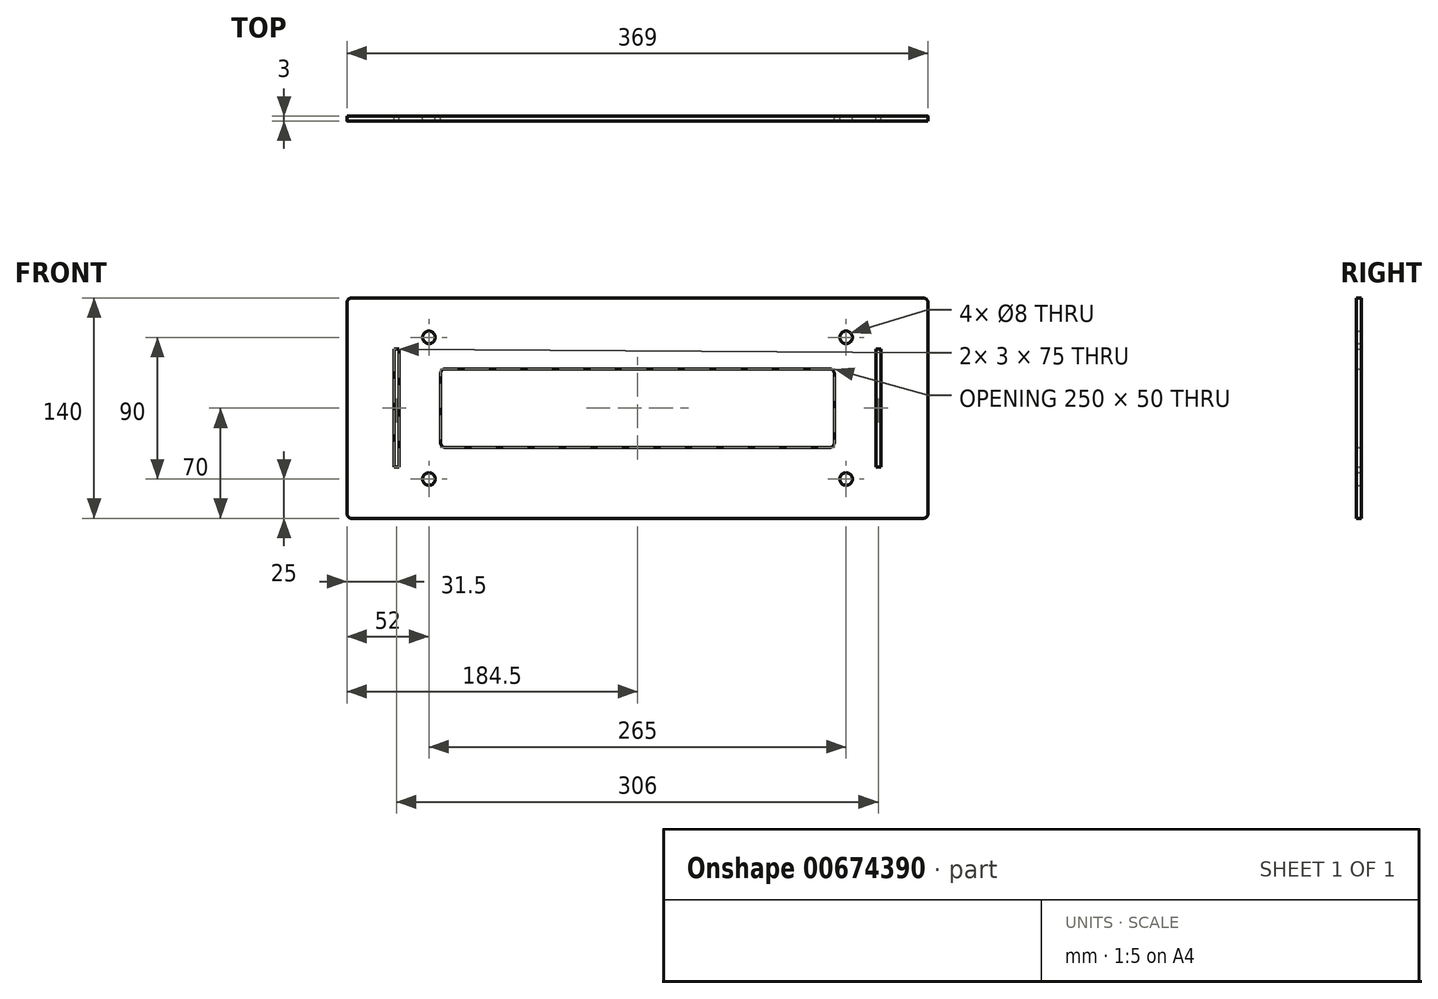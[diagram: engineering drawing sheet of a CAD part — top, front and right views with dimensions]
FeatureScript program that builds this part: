
annotation { "Feature Type Name" : "Feature", "Feature Type Description" : "" }
export const myFeature = defineFeature(function(context is Context, id is Id, definition is map)
    precondition{}
    {
        {
            var Q0;
            Q0=qCreatedBy(makeId("Front.planeOp"),FACE);
            var sketch = newSketch(context, id + "F0", { "sketchPlane" : qUnion([Q0])});
            skLineSegment(sketch, "E0.bottom", {"start": v(181.5, -70) * mm, "end": v(-181.5, -70) * mm});
            skLineSegment(sketch, "E0.top", {"start": v(181.5, 70) * mm, "end": v(-181.5, 70) * mm});
            skLineSegment(sketch, "E0.left", {"start": v(184.5, -67) * mm, "end": v(184.5, 67) * mm});
            skLineSegment(sketch, "E0.right", {"start": v(-184.5, -67) * mm, "end": v(-184.5, 67) * mm});
            skPoint(sketch, "E0.middle", {"position": v(0, 0) * mm});
            skLineSegment(sketch, "E1.bottom", {"start": v(-154.5, 37.5) * mm, "end": v(-151.5, 37.5) * mm});
            skLineSegment(sketch, "E1.top", {"start": v(-154.5, -37.5) * mm, "end": v(-151.5, -37.5) * mm});
            skLineSegment(sketch, "E1.left", {"start": v(-154.5, 37.5) * mm, "end": v(-154.5, -37.5) * mm});
            skLineSegment(sketch, "E1.right", {"start": v(-151.5, 37.5) * mm, "end": v(-151.5, -37.5) * mm});
            skLineSegment(sketch, "E2.MirrorCS", {"start": v(154.5, 37.5) * mm, "end": v(151.5, 37.5) * mm});
            skLineSegment(sketch, "E3.MirrorCS", {"start": v(154.5, -37.5) * mm, "end": v(151.5, -37.5) * mm});
            skLineSegment(sketch, "E4.MirrorCS", {"start": v(151.5, 37.5) * mm, "end": v(151.5, -37.5) * mm});
            skLineSegment(sketch, "E5.MirrorCS", {"start": v(154.5, 37.5) * mm, "end": v(154.5, -37.5) * mm});
            skCircle(sketch, "E6", {"center": v(132.5, -45) * mm, "radius": 4 * mm});
            skCircle(sketch, "E7", {"center": v(132.5, 45) * mm, "radius": 4 * mm});
            skCircle(sketch, "E8", {"center": v(-132.5, 45) * mm, "radius": 4 * mm});
            skCircle(sketch, "E9", {"center": v(-132.5, -45) * mm, "radius": 4 * mm});
            skLineSegment(sketch, "E10.bottom", {"start": v(122, -25) * mm, "end": v(-122, -25) * mm});
            skLineSegment(sketch, "E10.top", {"start": v(122, 25) * mm, "end": v(-122, 25) * mm});
            skLineSegment(sketch, "E10.left", {"start": v(125, -22) * mm, "end": v(125, 22) * mm});
            skLineSegment(sketch, "E10.right", {"start": v(-125, -22) * mm, "end": v(-125, 22) * mm});
            skPoint(sketch, "E11.visualSharp", {"position": v(184.5, 70) * mm});
            skArc(sketch, "E11.filletArc", {"start": v(184.5, 67) * mm, "mid": v(183.62, 69.12) * mm, "end": v(181.5, 70) * mm});
            skPoint(sketch, "E12.visualSharp", {"position": v(184.5, -70) * mm});
            skArc(sketch, "E12.filletArc", {"start": v(181.5, -70) * mm, "mid": v(183.62, -69.12) * mm, "end": v(184.5, -67) * mm});
            skPoint(sketch, "E13.visualSharp", {"position": v(-184.5, -70) * mm});
            skArc(sketch, "E13.filletArc", {"start": v(-184.5, -67) * mm, "mid": v(-183.62, -69.12) * mm, "end": v(-181.5, -70) * mm});
            skPoint(sketch, "E14.visualSharp", {"position": v(-184.5, 70) * mm});
            skArc(sketch, "E14.filletArc", {"start": v(-181.5, 70) * mm, "mid": v(-183.62, 69.12) * mm, "end": v(-184.5, 67) * mm});
            skPoint(sketch, "E15.visualSharp", {"position": v(-125, 25) * mm});
            skArc(sketch, "E15.filletArc", {"start": v(-122, 25) * mm, "mid": v(-124.12, 24.12) * mm, "end": v(-125, 22) * mm});
            skPoint(sketch, "E16.visualSharp", {"position": v(-125, -25) * mm});
            skArc(sketch, "E16.filletArc", {"start": v(-125, -22) * mm, "mid": v(-124.12, -24.12) * mm, "end": v(-122, -25) * mm});
            skPoint(sketch, "E17.visualSharp", {"position": v(125, 25) * mm});
            skArc(sketch, "E17.filletArc", {"start": v(125, 22) * mm, "mid": v(124.12, 24.12) * mm, "end": v(122, 25) * mm});
            skPoint(sketch, "E18.visualSharp", {"position": v(125, -25) * mm});
            skArc(sketch, "E18.filletArc", {"start": v(122, -25) * mm, "mid": v(124.12, -24.12) * mm, "end": v(125, -22) * mm});
            skSolve(sketch);
        }
        {
            var Q0;
            Q0=makeQuery(id+"F0.imprint","IMPRINT",FACE,{"disambiguationData":[TD([[makeQuery(id+"F0.imprint","IMPRINT",EDGE,{"derivedFrom":sQuery(id+"F0.wireOp",EDGE,"E0.bottom")}),-1.0]])]});
            extrude(context, id + "F1", {"entities" : qUnion([Q0]), "depth" : 3 * mm, "offsetDistance" : 25 * mm});
        }
    });
